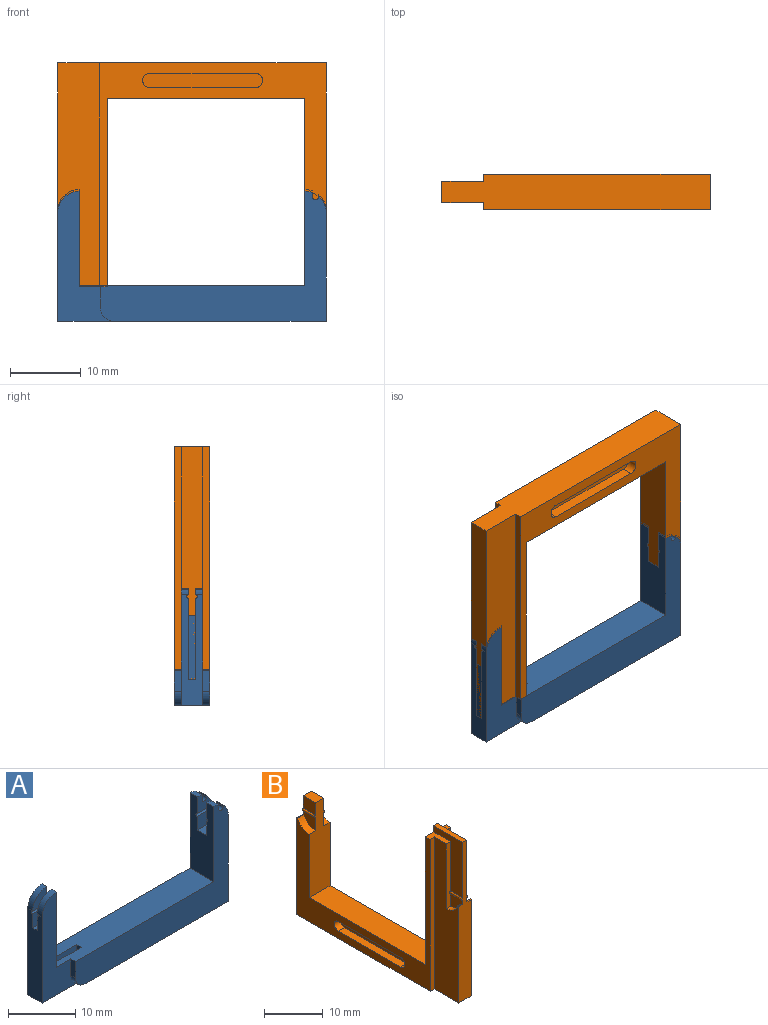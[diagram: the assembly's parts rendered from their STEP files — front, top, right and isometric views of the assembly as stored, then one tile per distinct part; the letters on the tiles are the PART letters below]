
ASSEMBLY  parts=2 mates=1
PART A: 46 faces, bbox 38x5x18.7 mm
  f0: plane 13.65x1mm, normal (1,0,0), area 13.5mm2, adj f3,f13,f14,f31,f34,f44,f45
  f1: plane 15.65x3mm, normal (-1,0,0), area 43.7mm2, adj f2,f3,f9,f10,f14,f29,f31,f37
  f2: plane 11.5x9.2mm, normal (0,1,0), area 27.6mm2, adj f1,f8,f12,f13,f35,f36,f37,f42
  f3: plane 11.5x9.2mm, normal (0,-1,0), area 27.6mm2, adj f0,f1,f8,f13,f35,f36,f37,f44
  f4: plane 3x3mm, normal (0,1,0), area 6.2mm2, adj f7,f17,f21,f25,f26,f28,f41
  f5: plane 3x3mm, normal (0,-1,0), area 6.2mm2, adj f7,f15,f20,f23,f24,f27,f40
  f6: plane 15.65x5mm, normal (1,0,0), area 72.1mm2, adj f10,f11,f15,f16,f17,f18,f19,f22
  f7: plane 13.65x5mm, normal (-1,0,0), area 56.1mm2, adj f4,f5,f11,f13,f16,f18,f19,f20
  f8: plane 9x1mm, normal (1,0,0), area 9mm2, adj f2,f3,f36,f37
  f9: cylinder r=3mm len=3mm, axis (0,-1,0), area 4.7mm2, adj f1,f12,f29,f33,f43
  f10: plane 38x5mm, normal (0,0,-1), area 174mm2, adj f1,f6,f11,f16,f29,f31,f38,f39
  f11: plane 32x18.65mm, normal (0,-1,0), area 197.3mm2, adj f6,f7,f10,f13,f17,f21,f25,f26
  f12: plane 13.65x1mm, normal (1,0,0), area 13.5mm2, adj f2,f9,f13,f29,f33,f42,f43
  f13: plane 32x5mm, normal (0,0,1), area 147.8mm2, adj f0,f2,f3,f7,f11,f12,f16,f29
  f14: cylinder r=3mm len=3mm, axis (0,-1,0), area 4.7mm2, adj f0,f1,f31,f34,f45
  f15: cylinder r=3mm len=2.28mm, axis (0,1,0), area 3.9mm2, adj f5,f6,f16,f24
  f16: plane 32x18.65mm, normal (0,1,0), area 197.3mm2, adj f6,f7,f10,f13,f15,f20,f23,f24
  f17: cylinder r=3mm len=2.28mm, axis (0,1,0), area 3.9mm2, adj f4,f6,f11,f25
  f18: plane 3x2.5mm, normal (0,1,0), area 7.5mm2, adj f6,f7,f22,f41
  f19: plane 3x2.5mm, normal (0,-1,0), area 7.5mm2, adj f6,f7,f22,f40
  f20: cylinder r=3mm len=1.5mm, axis (0,1,0), area 1.6mm2, adj f5,f7,f16,f23
  f21: cylinder r=3mm len=1.5mm, axis (0,1,0), area 1.6mm2, adj f4,f7,f11,f26
  f22: plane 3x2mm, normal (0,0,1), area 6mm2, adj f6,f7,f18,f19
  f23: plane 1.5x0.81mm, normal (1,0,0), area 1.2mm2, adj f5,f16,f20,f27
  f24: plane 1.5x0.28mm, normal (-1,0,0), area 0.4mm2, adj f5,f15,f16,f27
  f25: plane 1.5x0.28mm, normal (-1,0,0), area 0.4mm2, adj f4,f11,f17,f28
  f26: plane 1.5x0.81mm, normal (1,0,0), area 1.2mm2, adj f4,f11,f21,f28
  f27: cylinder r=0.45mm len=1.5mm, axis (0,1,0), area 2.1mm2, adj f5,f16,f23,f24
  f28: cylinder r=0.45mm len=1.5mm, axis (0,1,0), area 2.1mm2, adj f4,f11,f25,f26
  f29: plane 18.65x8mm, normal (0,-1,0), area 69.9mm2, adj f1,f9,f10,f12,f13,f30,f39
  f30: plane 3x1mm, normal (-1,0,0), area 3mm2, adj f11,f13,f29,f39
  f31: plane 18.65x8mm, normal (0,1,0), area 69.9mm2, adj f0,f1,f10,f13,f14,f32,f38
  f32: plane 3x1mm, normal (-1,0,0), area 3mm2, adj f13,f16,f31,f38
  f33: plane 3x3mm, normal (0,1,0), area 7.1mm2, adj f9,f12,f43
  f34: plane 3x3mm, normal (0,-1,0), area 7.1mm2, adj f0,f14,f45
  f35: plane 1.35x1mm, normal (-1,0,0), area 1.4mm2, adj f2,f3,f13,f36
  f36: plane 7.5x1mm, normal (0,0,1), area 7.5mm2, adj f2,f3,f8,f35
  f37: plane 1.7x1mm, normal (0,0,1), area 1.7mm2, adj f1,f2,f3,f8
  f38: cylinder r=2mm len=2mm, axis (0,-1,0), area 3.1mm2, adj f10,f16,f31,f32
  f39: cylinder r=2mm len=2mm, axis (0,-1,0), area 3.1mm2, adj f10,f11,f29,f30
  f40: cylinder r=0.25mm len=3mm, axis (1,0,0), area 2.4mm2, adj f5,f6,f7,f19
  f41: cylinder r=0.25mm len=3mm, axis (1,0,0), area 2.4mm2, adj f4,f6,f7,f18
  f42: cylinder r=0.25mm len=3mm, axis (-1,0,0), area 2.4mm2, adj f1,f2,f12,f43
  f43: plane 3x0.01mm, normal (0,0,-1), area 0mm2, adj f9,f12,f33,f42
  f44: cylinder r=0.25mm len=3mm, axis (-1,0,0), area 2.4mm2, adj f0,f1,f3,f45
  f45: plane 3x0.01mm, normal (0,0,-1), area 0mm2, adj f0,f14,f34,f44
PART B: 48 faces, bbox 5x38x33 mm
  f0: plane 32.1x31.7mm, normal (-1,0,0), area 198.2mm2, adj f8,f10,f12,f16,f18,f19,f24,f32
  f1: plane 32.1x31.7mm, normal (1,0,0), area 198.2mm2, adj f8,f10,f12,f14,f18,f19,f25,f28
  f2: plane 3x2.77mm, normal (1,0,0), area 6.4mm2, adj f3,f17,f23,f30,f37
  f3: plane 13.5x1mm, normal (0,-1,0), area 13.4mm2, adj f2,f13,f21,f23,f25,f37
  f4: plane 3x2.77mm, normal (-1,0,0), area 6.4mm2, adj f5,f17,f22,f31,f36
  f5: plane 13.5x1mm, normal (0,-1,0), area 13.4mm2, adj f4,f15,f20,f22,f24,f36
  f6: plane 3x2.77mm, normal (1,0,0), area 6.4mm2, adj f8,f10,f28,f29,f35
  f7: plane 3x2.77mm, normal (-1,0,0), area 6.4mm2, adj f8,f10,f32,f33,f34
  f8: plane 24x5mm, normal (0,1,0), area 108.5mm2, adj f0,f1,f6,f7,f9,f18,f26,f27
  f9: plane 3x2mm, normal (0,0,1), area 6mm2, adj f8,f10,f26,f27
  f10: plane 19x5mm, normal (0,-1,0), area 77.8mm2, adj f0,f1,f6,f7,f9,f19,f26,f27
  f11: plane 7x1mm, normal (0,0,1), area 7mm2, adj f12,f17,f20,f21
  f12: plane 28x5mm, normal (0,1,0), area 134.8mm2, adj f0,f1,f11,f19,f20,f21,f24,f25
  f13: plane 31.7x5.9mm, normal (1,0,0), area 148.4mm2, adj f3,f14,f17,f18,f23,f25,f30
  f14: plane 31.7x1mm, normal (0,-1,0), area 31.7mm2, adj f1,f13,f18,f25
  f15: plane 31.7x5.9mm, normal (-1,0,0), area 148.4mm2, adj f5,f16,f17,f18,f22,f24,f31
  f16: plane 31.7x1mm, normal (0,-1,0), area 31.7mm2, adj f0,f15,f18,f24
  f17: plane 33x3mm, normal (0,-1,0), area 73.4mm2, adj f2,f4,f11,f13,f15,f18,f20,f21
  f18: plane 38x5mm, normal (0,0,-1), area 178.2mm2, adj f0,f1,f8,f13,f14,f15,f16,f17
  f19: plane 28x5mm, normal (0,0,1), area 140mm2, adj f0,f1,f10,f12
  f20: plane 11.57x7mm, normal (-1,0,0), area 39.9mm2, adj f5,f11,f12,f17,f24,f36
  f21: plane 11.57x7mm, normal (1,0,0), area 39.9mm2, adj f3,f11,f12,f17,f25,f37
  f22: cylinder r=3mm len=2.81mm, axis (-1,0,0), area 3.6mm2, adj f4,f5,f15,f31
  f23: cylinder r=3mm len=2.81mm, axis (1,0,0), area 3.6mm2, adj f2,f3,f13,f30
  f24: plane 4x2mm, normal (0,0,1), area 5.1mm2, adj f0,f5,f12,f15,f16,f20
  f25: plane 4x2mm, normal (0,0,1), area 5.1mm2, adj f1,f3,f12,f13,f14,f21
  f26: plane 3x2.57mm, normal (-1,0,0), area 7.7mm2, adj f8,f9,f10,f34
  f27: plane 3x2.57mm, normal (1,0,0), area 7.7mm2, adj f8,f9,f10,f35
  f28: cylinder r=3mm len=2.81mm, axis (1,0,0), area 5.4mm2, adj f1,f6,f10,f29
  f29: cylinder r=0.1mm len=1.5mm, axis (1,0,0), area 0.4mm2, adj f1,f6,f8,f28
  f30: cylinder r=0.1mm len=1mm, axis (1,0,0), area 0.3mm2, adj f2,f13,f17,f23
  f31: cylinder r=0.1mm len=1mm, axis (-1,0,0), area 0.3mm2, adj f4,f15,f17,f22
  f32: cylinder r=3mm len=2.81mm, axis (-1,0,0), area 5.4mm2, adj f0,f7,f10,f33
  f33: cylinder r=0.1mm len=1.5mm, axis (-1,0,0), area 0.4mm2, adj f0,f7,f8,f32
  f34: cylinder r=0.23mm len=3mm, axis (0,-1,0), area 2.2mm2, adj f7,f8,f10,f26
  f35: cylinder r=0.23mm len=3mm, axis (0,-1,0), area 2.2mm2, adj f6,f8,f10,f27
  f36: cylinder r=0.23mm len=3mm, axis (0,1,0), area 2.2mm2, adj f4,f5,f17,f20
  f37: cylinder r=0.23mm len=3mm, axis (0,1,0), area 2.2mm2, adj f2,f3,f17,f21
  f38: plane 15x1.5mm, normal (0,0,-1), area 22.5mm2, adj f1,f39,f41,f42
  f39: cylinder r=1mm len=2mm, axis (1,0,0), area 4.7mm2, adj f1,f38,f40,f42
  f40: plane 15x1.5mm, normal (0,0,1), area 22.5mm2, adj f1,f39,f41,f42
  f41: cylinder r=1mm len=2mm, axis (1,0,0), area 4.7mm2, adj f1,f38,f40,f42
  f42: plane 17x2mm, normal (1,0,0), area 33.1mm2, adj f38,f39,f40,f41
  f43: plane 15x1.5mm, normal (0,0,-1), area 22.5mm2, adj f0,f44,f46,f47
  f44: cylinder r=1mm len=2mm, axis (-1,0,0), area 4.7mm2, adj f0,f43,f45,f47
  f45: plane 15x1.5mm, normal (0,0,1), area 22.5mm2, adj f0,f44,f46,f47
  f46: cylinder r=1mm len=2mm, axis (-1,0,0), area 4.7mm2, adj f0,f43,f45,f47
  f47: plane 17x2mm, normal (-1,0,0), area 33.1mm2, adj f43,f44,f45,f46
PLACE A at identity
PLACE B rot(axis=(0.71,0.71,0),180deg) t=(38,-0.01,23.43)mm
MATE fastened B.f35 <-> A.f40  axis (1,0,0) through (38,1,15.4)mm
